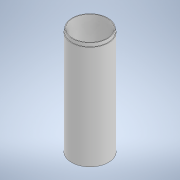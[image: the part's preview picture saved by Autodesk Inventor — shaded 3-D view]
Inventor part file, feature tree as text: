
AUTODESK INVENTOR PART (.ipt)
format: ipt  version: 2020.3 (Build 243373000, 373)  size: 108,544 bytes
history: native  units: mm
features: extrude x2, sketch x1
ambient origin geometry x8: Origin, YZ Plane, XZ Plane, XY Plane, X Axis, Y Axis, Z Axis, Center Point
bodies: Solid1 (feature_tree)
feature tree (3):
  sketch  "Sketch1"  dims[d0=51.8mm d1=50.0mm d2=53.6mm d3=150.0mm d4=0.0mm d5=70.0mm d6=80.0mm d7=0.0mm d8=0.0mm]
  extrude  "Extrusion1"  Depth=70.0mm TaperAngle=0.0deg
  extrude  "Extrusion2"  [1 undecoded]
note: 1 required parameter value undecoded (feature->parameter linkage not recoverable at this tier; creation-order binding heuristic only, values carry confidence <= 0.55)
